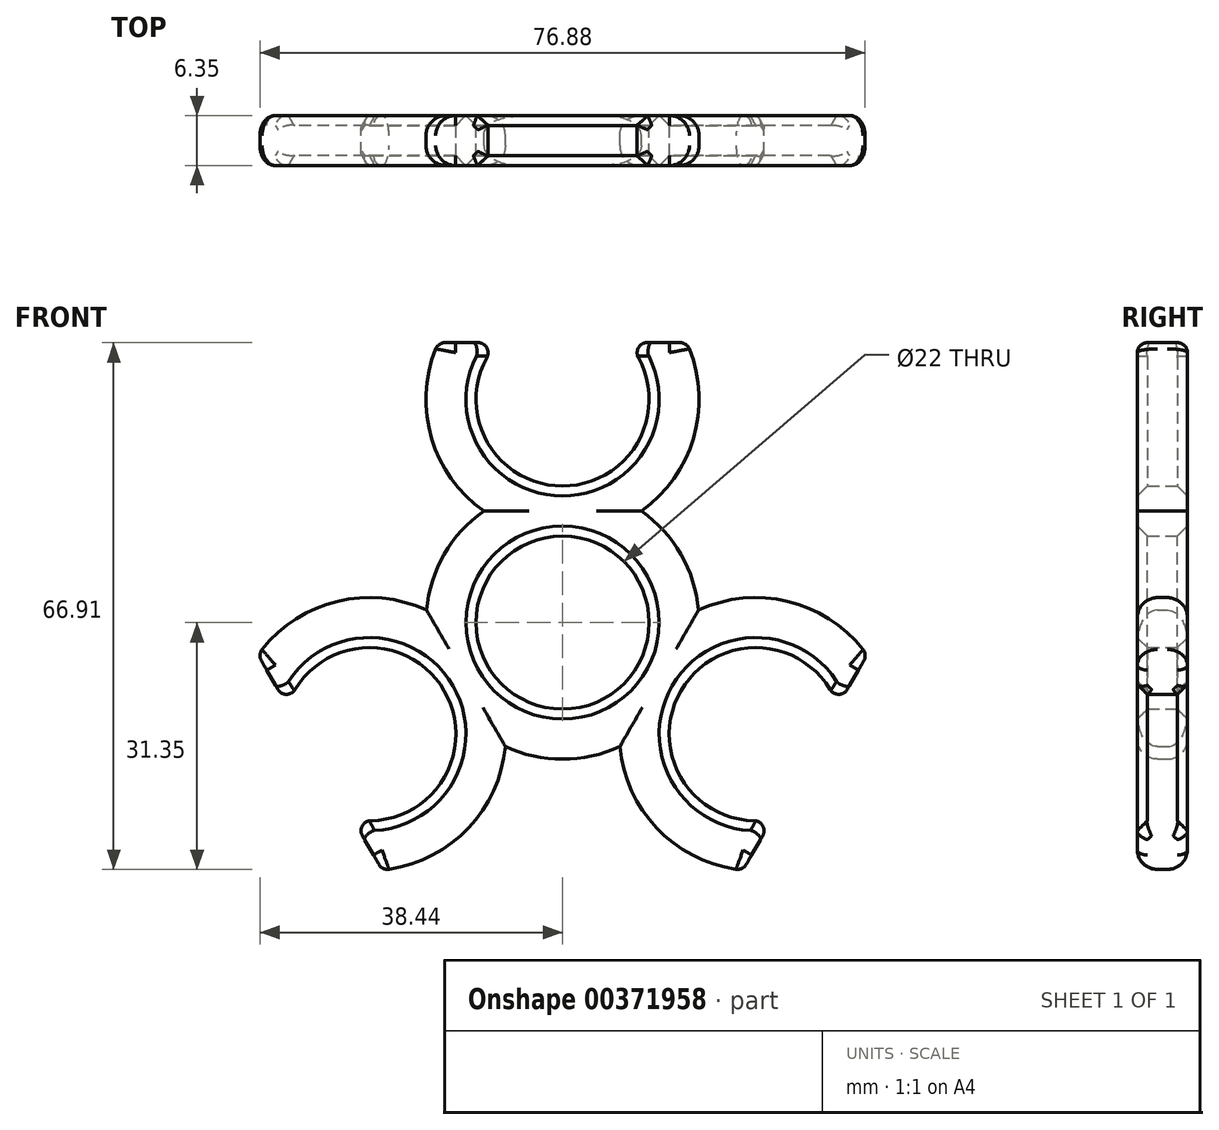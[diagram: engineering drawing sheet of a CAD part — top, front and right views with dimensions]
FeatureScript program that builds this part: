
annotation { "Feature Type Name" : "Feature", "Feature Type Description" : "" }
export const myFeature = defineFeature(function(context is Context, id is Id, definition is map)
    precondition{}
    {
        {
            var Q0;
            Q0=qCreatedBy(makeId("Front.planeOp"),FACE);
            var sketch = newSketch(context, id + "F0", { "sketchPlane" : qUnion([Q0])});
            skPoint(sketch, "E0.cCircle.center.orphan", {"position": v(0, 0) * mm});
            skCircle(sketch, "E1", {"center": v(0, 0) * mm, "radius": 11 * mm});
            skPoint(sketch, "E2", {"position": v(0, 28.35) * mm});
            skPoint(sketch, "E3", {"position": v(24.55, -14.17) * mm});
            skPoint(sketch, "E4", {"position": v(-24.55, -14.17) * mm});
            skCircle(sketch, "E5", {"center": v(0, 28.35) * mm, "radius": 11 * mm});
            skCircle(sketch, "E6", {"center": v(24.55, -14.17) * mm, "radius": 11 * mm});
            skCircle(sketch, "E7", {"center": v(-24.55, -14.17) * mm, "radius": 11 * mm});
            skArc(sketch, "E8", {"start": v(10, 14.17) * mm, "mid": v(0, 45.7) * mm, "end": v(-10, 14.17) * mm});
            skArc(sketch, "E9", {"start": v(-10, 14.17) * mm, "mid": v(-15.02, 8.67) * mm, "end": v(-17.28, 1.58) * mm});
            skArc(sketch, "E10", {"start": v(7.27, -15.75) * mm, "mid": v(39.57, -22.85) * mm, "end": v(17.28, 1.58) * mm});
            skArc(sketch, "E11", {"start": v(-17.28, 1.58) * mm, "mid": v(-39.57, -22.85) * mm, "end": v(-7.27, -15.75) * mm});
            skArc(sketch, "E12.trimOffspring", {"start": v(-7.27, -15.75) * mm, "mid": v(0, -17.35) * mm, "end": v(7.27, -15.75) * mm});
            skArc(sketch, "E13.trimOffspring", {"start": v(17.28, 1.58) * mm, "mid": v(15.02, 8.67) * mm, "end": v(10, 14.17) * mm});
            skSolve(sketch);
        }
        {
            var Q0;
            Q0 = qSketchRegion(id + "F0", true);
            extrude(context, id + "F1", {"entities" : qUnion([Q0]), "depth" : 6.35 * mm, "offsetDistance" : 25.4 * mm});
        }
        {
            var Q0;
            Q0=makeQuery(id+"F1.opExtrude","CAP_EDGE",EDGE,{"disambiguationData":[OSD([sQuery(id+"F0.wireOp",EDGE,"E8")])],"isStart":true});
            var Q1;
            Q1=makeQuery(id+"F1.opExtrude","CAP_EDGE",EDGE,{"disambiguationData":[OSD([sQuery(id+"F0.wireOp",EDGE,"E8")])],"isStart":false});
            var Q2;
            Q2=makeQuery(id+"F1.opExtrude","CAP_EDGE",EDGE,{"disambiguationData":[OSD([sQuery(id+"F0.wireOp",EDGE,"E13.trimOffspring")])],"isStart":false});
            var Q3;
            Q3=makeQuery(id+"F1.opExtrude","CAP_EDGE",EDGE,{"disambiguationData":[OSD([sQuery(id+"F0.wireOp",EDGE,"E13.trimOffspring")])],"isStart":true});
            var Q4;
            Q4=makeQuery(id+"F1.opExtrude","CAP_EDGE",EDGE,{"disambiguationData":[OSD([sQuery(id+"F0.wireOp",EDGE,"E10")])],"isStart":false});
            var Q5;
            Q5=makeQuery(id+"F1.opExtrude","CAP_EDGE",EDGE,{"disambiguationData":[OSD([sQuery(id+"F0.wireOp",EDGE,"E10")])],"isStart":true});
            var Q6;
            Q6=makeQuery(id+"F1.opExtrude","CAP_EDGE",EDGE,{"disambiguationData":[OSD([sQuery(id+"F0.wireOp",EDGE,"E12.trimOffspring")])],"isStart":false});
            var Q7;
            Q7=makeQuery(id+"F1.opExtrude","CAP_EDGE",EDGE,{"disambiguationData":[OSD([sQuery(id+"F0.wireOp",EDGE,"E9")])],"isStart":false});
            var Q8;
            Q8=makeQuery(id+"F1.opExtrude","CAP_EDGE",EDGE,{"disambiguationData":[OSD([sQuery(id+"F0.wireOp",EDGE,"E9")])],"isStart":true});
            var Q9;
            Q9=makeQuery(id+"F1.opExtrude","CAP_EDGE",EDGE,{"disambiguationData":[OSD([sQuery(id+"F0.wireOp",EDGE,"E11")])],"isStart":false});
            var Q10;
            Q10=makeQuery(id+"F1.opExtrude","CAP_EDGE",EDGE,{"disambiguationData":[OSD([sQuery(id+"F0.wireOp",EDGE,"E11")])],"isStart":true});
            var Q11;
            Q11=makeQuery(id+"F1.opExtrude","CAP_EDGE",EDGE,{"disambiguationData":[OSD([sQuery(id+"F0.wireOp",EDGE,"E12.trimOffspring")])],"isStart":true});
            fillet(context, id + "F2", {"entities" : qUnion([Q0, Q1, Q2, Q3, Q4, Q5, Q6, Q7, Q8, Q9, Q10, Q11]), "radius" : 2.54 * mm, "tangentPropagation" : true, "allowEdgeOverflow" : false});
        }
        {
            var Q0;
            Q0=makeQuery(id+"F1.opExtrude","CAP_EDGE",EDGE,{"disambiguationData":[OSD([sQuery(id+"F0.wireOp",EDGE,"E6")])],"isStart":true});
            var Q1;
            Q1=makeQuery(id+"F1.opExtrude","CAP_EDGE",EDGE,{"disambiguationData":[OSD([sQuery(id+"F0.wireOp",EDGE,"E6")])],"isStart":false});
            var Q2;
            Q2=makeQuery(id+"F1.opExtrude","CAP_EDGE",EDGE,{"disambiguationData":[OSD([sQuery(id+"F0.wireOp",EDGE,"E1")])],"isStart":true});
            var Q3;
            Q3=makeQuery(id+"F1.opExtrude","CAP_EDGE",EDGE,{"disambiguationData":[OSD([sQuery(id+"F0.wireOp",EDGE,"E1")])],"isStart":false});
            var Q4;
            Q4=makeQuery(id+"F1.opExtrude","CAP_EDGE",EDGE,{"disambiguationData":[OSD([sQuery(id+"F0.wireOp",EDGE,"E7")])],"isStart":true});
            var Q5;
            Q5=makeQuery(id+"F1.opExtrude","CAP_EDGE",EDGE,{"disambiguationData":[OSD([sQuery(id+"F0.wireOp",EDGE,"E7")])],"isStart":false});
            var Q6;
            Q6=makeQuery(id+"F1.opExtrude","CAP_EDGE",EDGE,{"disambiguationData":[OSD([sQuery(id+"F0.wireOp",EDGE,"E5")])],"isStart":true});
            var Q7;
            Q7=makeQuery(id+"F1.opExtrude","CAP_EDGE",EDGE,{"disambiguationData":[OSD([sQuery(id+"F0.wireOp",EDGE,"E5")])],"isStart":false});
            chamfer(context, id + "F3", {"entities" : qUnion([Q0, Q1, Q2, Q3, Q4, Q5, Q6, Q7]), "width" : 1.27 * mm, "tangentPropagation" : true});
        }
        {
            var Q0;
            Q0=qCreatedBy(makeId("Front.planeOp"),FACE);
            var sketch = newSketch(context, id + "F4", { "sketchPlane" : qUnion([Q0])});
            skCircle(sketch, "E14", {"center": v(-74.39, 62.84) * mm, "radius": 4.47 * mm});
            skSolve(sketch);
        }
        {
            var Q0;
            Q0 = qSketchRegion(id + "F4", true);
            extrude(context, id + "F5", {"entities" : qUnion([Q0]), "depth" : 25.4 * mm, "offsetDistance" : 25.4 * mm});
        }
        {
            var Q0;
            Q0=makeQuery(id+"F5.opExtrude","CAP_FACE",FACE,{"disambiguationData":[OSD([sQuery(id+"F4.wireOp",EDGE,"E14")])],"isStart":false});
            var sketch = newSketch(context, id + "F6", { "sketchPlane" : qUnion([Q0])});
            skPoint(sketch, "E15", {"position": v(0, 35.56) * mm});
            skPoint(sketch, "E16", {"position": v(30.8, -17.78) * mm});
            skPoint(sketch, "E17", {"position": v(-30.8, -17.78) * mm});
            skLineSegment(sketch, "E18", {"start": v(-25.5, 35.56) * mm, "end": v(31.13, 35.56) * mm});
            skLineSegment(sketch, "E19", {"start": v(31.13, 35.56) * mm, "end": v(31.13, 53.15) * mm});
            skLineSegment(sketch, "E20", {"start": v(31.13, 53.15) * mm, "end": v(-25.5, 53.15) * mm});
            skLineSegment(sketch, "E21", {"start": v(-25.5, 53.15) * mm, "end": v(-25.5, 35.56) * mm});
            skLineSegment(sketch, "E22", {"start": v(30.8, -17.78) * mm, "end": v(47.73, 11.55) * mm});
            skLineSegment(sketch, "E23", {"start": v(47.73, 11.55) * mm, "end": v(61.6, 3.55) * mm});
            skLineSegment(sketch, "E24", {"start": v(61.6, 3.55) * mm, "end": v(34.38, -43.58) * mm});
            skLineSegment(sketch, "E25", {"start": v(30.8, -17.78) * mm, "end": v(20.24, -36.06) * mm});
            skLineSegment(sketch, "E26", {"start": v(20.24, -36.06) * mm, "end": v(34.38, -43.58) * mm});
            skLineSegment(sketch, "E27", {"start": v(-30.8, -17.78) * mm, "end": v(-44.55, 6.05) * mm});
            skLineSegment(sketch, "E28", {"start": v(-44.55, 6.05) * mm, "end": v(-58.44, -1.96) * mm});
            skLineSegment(sketch, "E29", {"start": v(-58.44, -1.96) * mm, "end": v(-34.4, -43.58) * mm});
            skLineSegment(sketch, "E30", {"start": v(-30.8, -17.78) * mm, "end": v(-18.85, -38.48) * mm});
            skLineSegment(sketch, "E31", {"start": v(-18.85, -38.48) * mm, "end": v(-34.4, -43.58) * mm});
            skPoint(sketch, "E32.orphan", {"position": v(0, 0) * mm});
            skPoint(sketch, "E33.end.orphan", {"position": v(61.6, -35.56) * mm});
            skSolve(sketch);
        }
        {
            var Q0;
            Q0 = qSketchRegion(id + "F6", true);
            extrude(context, id + "F7", {"entities" : qUnion([Q0]), "operationType" : NewBodyOperationType.REMOVE, "oppositeDirection" : true, "depth" : 25.4 * mm, "offsetDistance" : 25.4 * mm});
        }
        {
            var Q0;
            Q0=makeQuery(id+"F7.boolean.opBoolean","COPY",FACE,{"disambiguationData":[OD(1.0)],"derivedFrom":makeQuery(id+"F7.opExtrude","SWEPT_FACE",FACE,{"disambiguationData":[OSD([sQuery(id+"F6.wireOp",EDGE,"E18")])]})});
            var Q1;
            Q1=makeQuery(id+"F7.boolean.opBoolean","COPY",FACE,{"disambiguationData":[OD(0.0)],"derivedFrom":makeQuery(id+"F7.opExtrude","SWEPT_FACE",FACE,{"disambiguationData":[OSD([sQuery(id+"F6.wireOp",EDGE,"E18")])]})});
            var Q2;
            Q2=makeQuery(id+"F7.boolean.opBoolean","COPY",FACE,{"disambiguationData":[OD(1.0)],"derivedFrom":makeQuery(id+"F7.opExtrude","SWEPT_FACE",FACE,{"disambiguationData":[OSD([sQuery(id+"F6.wireOp",EDGE,"E27"),sQuery(id+"F6.wireOp",EDGE,"E30")])]})});
            var Q3;
            Q3=makeQuery(id+"F7.boolean.opBoolean","COPY",FACE,{"disambiguationData":[OD(0.0)],"derivedFrom":makeQuery(id+"F7.opExtrude","SWEPT_FACE",FACE,{"disambiguationData":[OSD([sQuery(id+"F6.wireOp",EDGE,"E27"),sQuery(id+"F6.wireOp",EDGE,"E30")])]})});
            var Q4;
            Q4=makeQuery(id+"F7.boolean.opBoolean","COPY",FACE,{"disambiguationData":[OD(1.0)],"derivedFrom":makeQuery(id+"F7.opExtrude","SWEPT_FACE",FACE,{"disambiguationData":[OSD([sQuery(id+"F6.wireOp",EDGE,"E22"),sQuery(id+"F6.wireOp",EDGE,"E25")])]})});
            var Q5;
            Q5=makeQuery(id+"F7.boolean.opBoolean","COPY",FACE,{"disambiguationData":[OD(0.0)],"derivedFrom":makeQuery(id+"F7.opExtrude","SWEPT_FACE",FACE,{"disambiguationData":[OSD([sQuery(id+"F6.wireOp",EDGE,"E22"),sQuery(id+"F6.wireOp",EDGE,"E25")])]})});
            fillet(context, id + "F8", {"entities" : qUnion([Q0, Q1, Q2, Q3, Q4, Q5]), "radius" : 1.27 * mm, "tangentPropagation" : true, "allowEdgeOverflow" : false});
        }
        {
            var Q0;
            Q0=makeQuery(id+"F5.opExtrude","SWEPT_BODY",BODY,{"disambiguationData":[OSD([sQuery(id+"F4.wireOp",EDGE,"E14")])]});
            deleteBodies(context, id + "F9", {"entities" : qUnion([Q0])});
        }
    });
